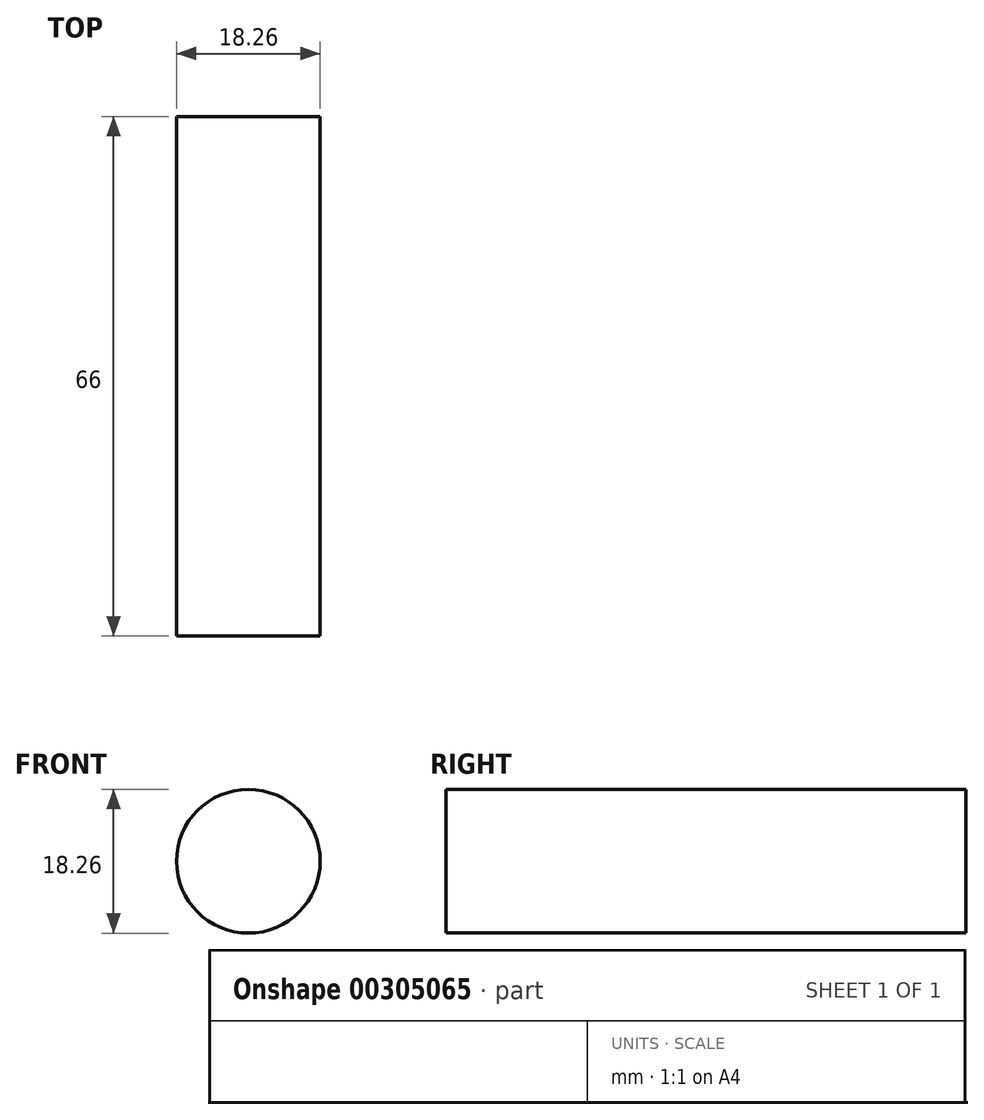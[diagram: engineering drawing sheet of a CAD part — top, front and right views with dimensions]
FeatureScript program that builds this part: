
annotation { "Feature Type Name" : "Feature", "Feature Type Description" : "" }
export const myFeature = defineFeature(function(context is Context, id is Id, definition is map)
    precondition{}
    {
        {
            var Q0;
            Q0=qCreatedBy(makeId("Front.planeOp"),FACE);
            var sketch = newSketch(context, id + "F0", { "sketchPlane" : qUnion([Q0])});
            skCircle(sketch, "E0", {"center": v(0, 0) * mm, "radius": 9.12 * mm});
            skSolve(sketch);
        }
        {
            var Q0;
            Q0 = qSketchRegion(id + "F0", true);
            extrude(context, id + "F1", {"entities" : qUnion([Q0]), "depth" : 66 * mm});
        }
    });
